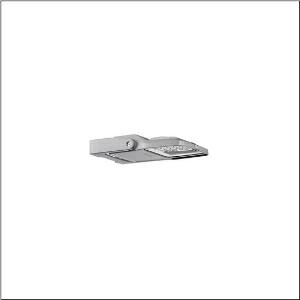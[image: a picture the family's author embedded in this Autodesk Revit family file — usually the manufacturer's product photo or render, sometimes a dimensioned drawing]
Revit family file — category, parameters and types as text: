
# Revit family: floodlight_fl_21_iq_micro___pl64_5xa7761a2e2a_9d46
name_source: partatom
category: Lighting Fixtures
units: mm (PartAtom-declared; Revit-internal decimal feet)

## family parameters
Cut with Voids When Loaded = No
Host = Face
Light Source = No
Part Type = Normal
Room Calculation Point = No
Round Connector Dimension = Use Diameter
Shared = No

## types (1)
- --- (1 x LED, 2870 lm, 23.1 W, 3000K)
    Apparent Load = 23 VA
    CIE Flux Codes = 28 80 98 100 100
    Color Rendering = 70
    Color Temperature = 3000K
    Default Elevation = 1800 mm
    Description = Floodlight FL 21 iQ micro, floodlight, primary light control with lens, of PMMA, primary optical cover: protective disc, of toughened safety glass, transparent, light distribution: PL64, light emission: direct distribution, installation type: surface-mounted, LED, High Power LED, rated luminous flux: 2.870lm, luminous efficacy: 124lm/W, light colour: 730, colour temperature: 3000K, control: optimised constant luminous flux control (CLO 2.0), Desk-Remote (wireless, voltage-free reading and setting of iQ features in the workshop via application-optimized NFC function/RFID function), Light-Fading, Smart-Wire, Night-Set, Lumen-Switch, Temp-Guard, Auto-Match, with terminal, 6-pole, mains connection: 220..240V, AC, 50/60Hz, start of lifetime: 23W, end of service life: 24W, reduction: 11W, luminaire housing, of diecast aluminium, powder-coated, Siteco® metallic grey (DB 702S), corrosivity category C5 mid according to DIN EN ISO 12944, sealing non-destructively replaceable, design bracket, of diecast aluminium, powder-coated, Siteco® metallic grey (DB 702S), protection rating (complete): IP66, insulation class (complete): insulation class II (safety insulation), certification: CE, ENEC, VDE, protection symbol: D, impact resistance: IK07, permissible operating ambient temperature: -40..+40°C, permissible operating ambient temperature for outdoor applications: -40..+50°C, standard: DIN EN 12944, LABS conformity tested according to VDMA 24364:2018-05, packaging unit: 1 piece

Light Distribution: PL64
    Height = 65 mm
    Lamp = 1 x LED
    Lamp Light Flux = 2870 lm
    Lamp Power = 23.1 W
    Lamp count = 1
    Length = 312 mm
    Luminous efficacy = 124 lm/W
    Manufacturer = Siteco
    ModVariant = No
    Model = 5XA7761A2E2A
    Mounting Place = Wall
    Mounting Type = Surface mounted
    Number of Poles = 1
    OnlyDefault = Yes
    Power Factor = 1
    Product Name = Floodlight FL 21 iQ micro | PL64
    Product group = floodlight | wall mounted
    ProductGroupID = 2001
    Protection Class = Protection class II
    Protection Degree = IP 66
    RLX_Detail_Level = 1
    RLX_Emergency_Light_Flux = 0 lm
    RLX_Emergency_Type = 0
    RLX_Emergency_Type_DB = No
    RlxData = <blob elided: 97317 chars, md5=4d0bae40>
    Socket = socket
    Standby Power = 0 W
    System Light Flux = 2870 lm
    System Power = 23 W
    Type Comments = factory setting: luminous flux: 100 % | dim-lin: 254 | 455 mA
    Type Image = l_1006878.jpg
    URL = http://relux.com
    VarID = @adj_152403
    Voltage = 0 V
    Weight = 0.00 kg
    Width = 230 mm

## geometry (parser evidence)
native form markers: Blend x4, Sweep x12
no freeform markers — native parametric forms only
